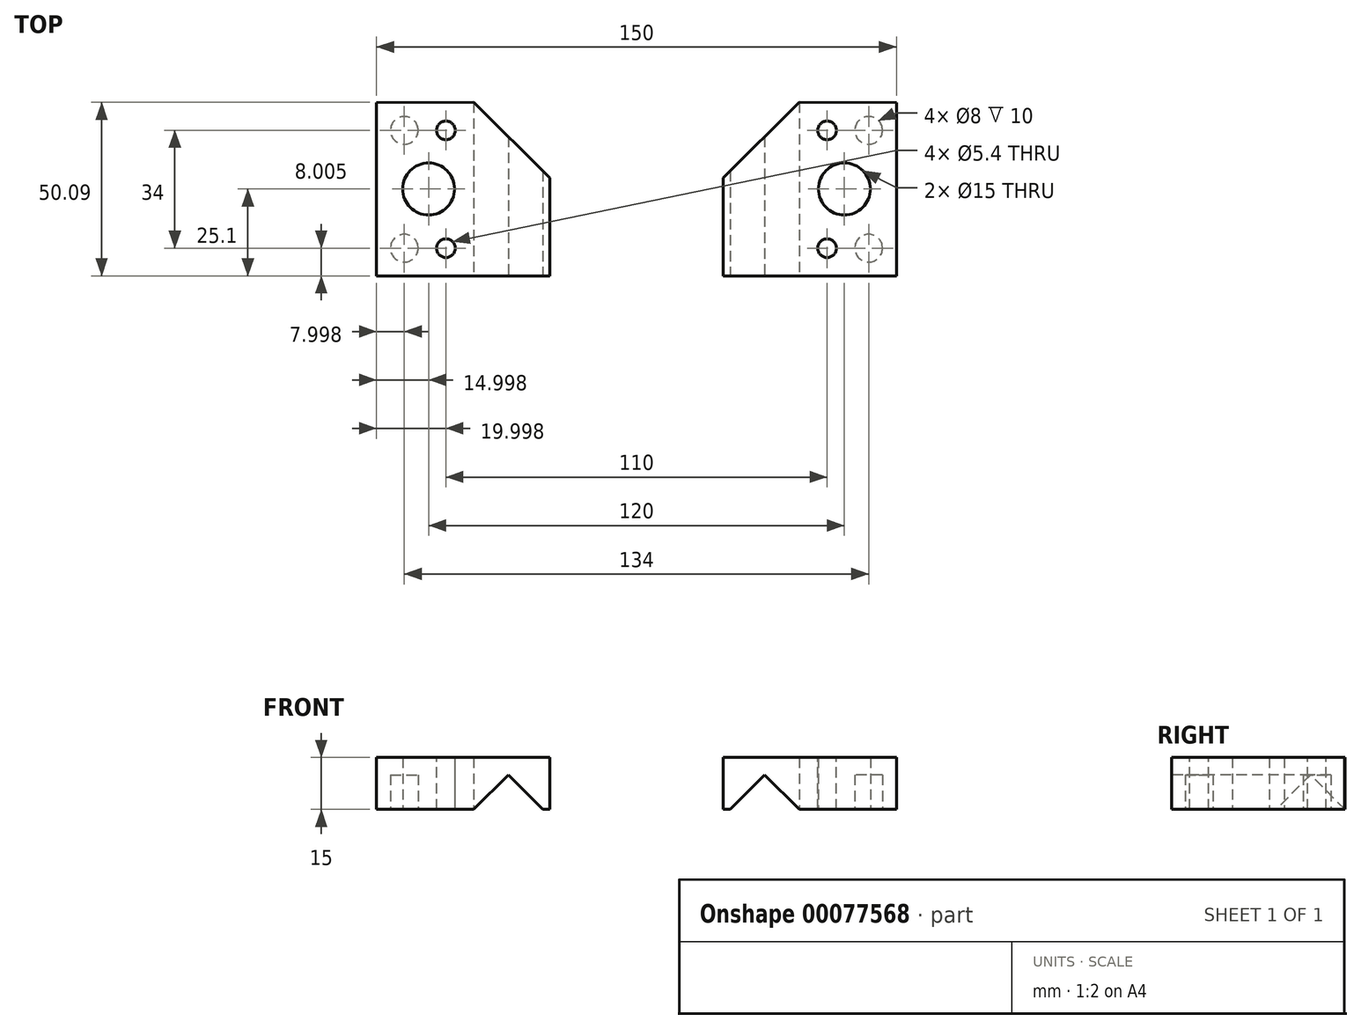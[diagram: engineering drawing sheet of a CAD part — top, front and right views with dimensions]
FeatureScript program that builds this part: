
annotation { "Feature Type Name" : "Feature", "Feature Type Description" : "" }
export const myFeature = defineFeature(function(context is Context, id is Id, definition is map)
    precondition{}
    {
        {
            var Q0;
            Q0=qCreatedBy(makeId("Top.planeOp"),FACE);
            var sketch = newSketch(context, id + "F0", { "sketchPlane" : qUnion([Q0])});
            skLineSegment(sketch, "E0.bottom", {"start": v(24.6, 20.06) * mm, "end": v(-25.4, 19.9) * mm});
            skLineSegment(sketch, "E0.top", {"start": v(24.6, -30.1) * mm, "end": v(-25.4, -30.1) * mm});
            skLineSegment(sketch, "E0.left", {"start": v(24.6, 20.06) * mm, "end": v(24.6, -30.1) * mm});
            skLineSegment(sketch, "E0.right", {"start": v(-25.4, 19.9) * mm, "end": v(-25.4, -30.1) * mm});
            skPoint(sketch, "E0.middle", {"position": v(0, 0) * mm});
            skSolve(sketch);
        }
        {
            var Q0;
            Q0 = qSketchRegion(id + "F0", true);
            extrude(context, id + "F1", {"entities" : qUnion([Q0]), "depth" : 15 * mm});
        }
        {
            var Q0;
            Q0=makeQuery(id+"F1.opExtrude","SWEPT_FACE",FACE,{"disambiguationData":[OSD([sQuery(id+"F0.wireOp",EDGE,"E0.top")])]});
            var sketch = newSketch(context, id + "F2", { "sketchPlane" : qUnion([Q0])});
            skLineSegment(sketch, "E1", {"start": v(22.6, 0) * mm, "end": v(12.6, 10) * mm});
            skPoint(sketch, "E1.endSnap0", {"position": v(20, 12.5) * mm});
            skLineSegment(sketch, "E2", {"start": v(12.6, 10) * mm, "end": v(2.6, 0) * mm});
            skLineSegment(sketch, "E3", {"start": v(2.6, 0) * mm, "end": v(22.6, 0) * mm});
            skSolve(sketch);
        }
        {
            var Q0;
            Q0=makeQuery(id+"F2.imprint","IMPRINT",FACE,{"disambiguationData":[TD([[makeQuery(id+"F2.imprint","IMPRINT",EDGE,{"derivedFrom":sQuery(id+"F2.wireOp",EDGE,"E1")}),1.0]])]});
            extrude(context, id + "F3", {"entities" : qUnion([Q0]), "operationType" : NewBodyOperationType.REMOVE, "endBound" : BoundingType.THROUGH_ALL, "oppositeDirection" : true, "depth" : 25 * mm});
        }
        {
            var Q0;
            {var subQ0=sQuery(id+"F0.wireOp",EDGE,"E0.bottom");var subQ1=sQuery(id+"F0.wireOp",EDGE,"E0.top");var subQ2=sQuery(id+"F0.wireOp",EDGE,"E0.right");Q0=makeQuery(id+"F3.boolean.opBoolean","SPLIT",FACE,{"disambiguationData":[TD([makeQuery(id+"F1.opExtrude","SWEPT_FACE",FACE,{"disambiguationData":[OSD([subQ2])]})])],"derivedFrom":makeQuery(id+"F1.opExtrude","CAP_FACE",FACE,{"disambiguationData":[OSD([subQ0,subQ1,sQuery(id+"F0.wireOp",EDGE,"E0.left"),subQ2])],"isStart":true})});}
            var sketch = newSketch(context, id + "F4", { "sketchPlane" : qUnion([Q0])});
            skCircle(sketch, "E4", {"center": v(-17.4, 22.1) * mm, "radius": 4 * mm});
            skCircle(sketch, "E5", {"center": v(-17.4, -11.9) * mm, "radius": 4 * mm});
            skSolve(sketch);
        }
        {
            var Q0;
            Q0 = qSketchRegion(id + "F4", true);
            extrude(context, id + "F5", {"entities" : qUnion([Q0]), "operationType" : NewBodyOperationType.REMOVE, "oppositeDirection" : true, "depth" : 10 * mm});
        }
        {
            var Q0;
            {var subQ0=sQuery(id+"F0.wireOp",EDGE,"E0.bottom");var subQ1=sQuery(id+"F0.wireOp",EDGE,"E0.top");var subQ2=sQuery(id+"F0.wireOp",EDGE,"E0.right");Q0=makeQuery(id+"F3.boolean.opBoolean","SPLIT",FACE,{"disambiguationData":[TD([makeQuery(id+"F1.opExtrude","SWEPT_FACE",FACE,{"disambiguationData":[OSD([subQ2])]})])],"derivedFrom":makeQuery(id+"F1.opExtrude","CAP_FACE",FACE,{"disambiguationData":[OSD([subQ0,subQ1,sQuery(id+"F0.wireOp",EDGE,"E0.left"),subQ2])],"isStart":true})});}
            var sketch = newSketch(context, id + "F6", { "sketchPlane" : qUnion([Q0])});
            skLineSegment(sketch, "E6", {"start": v(-10.4, 22) * mm, "end": v(-10.4, -12) * mm});
            skLineSegment(sketch, "E7", {"start": v(-4.4, 0) * mm, "end": v(-10.4, 5) * mm});
            skPoint(sketch, "E8", {"position": v(-10.4, 5) * mm});
            skPoint(sketch, "E9", {"position": v(3.86, -3.22) * mm});
            skCircle(sketch, "E10", {"center": v(-10.4, 5) * mm, "radius": 7.5 * mm});
            skLineSegment(sketch, "E11", {"start": v(-6, 12.5) * mm, "end": v(-23, 12.5) * mm});
            skLineSegment(sketch, "E12", {"start": v(-6, -2.5) * mm, "end": v(-23, -2.5) * mm});
            skSolve(sketch);
        }
        {
            var Q0;
            {var subQ0=sQuery(id+"F6.wireOp",EDGE,"E6");var subQ1=makeQuery(id+"F6.imprint","INTERSECT",VERTEX,{"derivedFrom":[subQ0,sQuery(id+"F6.wireOp",EDGE,"E7")]});Q0=makeQuery(id+"F6.imprint","IMPRINT",FACE,{"disambiguationData":[TD([[makeQuery(id+"F6.imprint","IMPRINT",EDGE,{"disambiguationData":[TD([[subQ1,1.0]])],"derivedFrom":subQ0}),-1.0]])]});}
            var Q1;
            {var subQ0=sQuery(id+"F6.wireOp",EDGE,"E7");var subQ1=sQuery(id+"F6.wireOp",EDGE,"E6");var subQ2=makeQuery(id+"F6.imprint","INTERSECT",VERTEX,{"derivedFrom":[subQ1,subQ0]});Q1=makeQuery(id+"F6.imprint","IMPRINT",FACE,{"disambiguationData":[TD([[makeQuery(id+"F6.imprint","IMPRINT",EDGE,{"disambiguationData":[TD([[subQ2,1.0]])],"derivedFrom":subQ0}),-1.0]])]});}
            var Q2;
            {var subQ0=sQuery(id+"F6.wireOp",EDGE,"E7");var subQ1=sQuery(id+"F6.wireOp",EDGE,"E6");var subQ2=makeQuery(id+"F6.imprint","INTERSECT",VERTEX,{"derivedFrom":[subQ1,subQ0]});Q2=makeQuery(id+"F6.imprint","IMPRINT",FACE,{"disambiguationData":[TD([[makeQuery(id+"F6.imprint","IMPRINT",EDGE,{"disambiguationData":[TD([[subQ2,1.0]])],"derivedFrom":subQ0}),1.0]])]});}
            var Q3;
            {var subQ0=sQuery(id+"F6.wireOp",EDGE,"E6");var subQ1=makeQuery(id+"F6.imprint","IMPRINT",VERTEX,{"derivedFrom":subQ0});Q3=makeQuery(id+"F6.imprint","IMPRINT",FACE,{"disambiguationData":[TD([[makeQuery(id+"F6.imprint","IMPRINT",EDGE,{"disambiguationData":[TD([[subQ1,1.0]])],"derivedFrom":subQ0}),1.0]])]});}
            extrude(context, id + "F7", {"entities" : qUnion([Q0, Q1, Q2, Q3]), "operationType" : NewBodyOperationType.REMOVE, "endBound" : BoundingType.THROUGH_ALL, "oppositeDirection" : true, "depth" : 25 * mm});
        }
        {
            var Q0;
            Q0=makeQuery(id+"F1.opExtrude","CAP_FACE",FACE,{"disambiguationData":[OSD([sQuery(id+"F0.wireOp",EDGE,"E0.bottom"),sQuery(id+"F0.wireOp",EDGE,"E0.top"),sQuery(id+"F0.wireOp",EDGE,"E0.left"),sQuery(id+"F0.wireOp",EDGE,"E0.right")])],"isStart":false});
            var sketch = newSketch(context, id + "F8", { "sketchPlane" : qUnion([Q0])});
            skPoint(sketch, "E13.positionSnap0", {"position": v(-5.4, -22.1) * mm});
            skLineSegment(sketch, "E14", {"start": v(-5.4, -22.1) * mm, "end": v(-5.4, 11.9) * mm});
            skPoint(sketch, "E15", {"position": v(-5.4, 11.9) * mm});
            skSolve(sketch);
        }
        {
            var Q0;
            Q0=sQuery(id+"F8.wireOp",VERTEX,"E13.positionSnap0");
            var Q1;
            Q1=sQuery(id+"F8.wireOp",VERTEX,"E15");
            var Q2;
            Q2=makeQuery(id+"F1.opExtrude","SWEPT_BODY",BODY,{"disambiguationData":[OSD([sQuery(id+"F0.wireOp",EDGE,"E0.bottom"),sQuery(id+"F0.wireOp",EDGE,"E0.top"),sQuery(id+"F0.wireOp",EDGE,"E0.left"),sQuery(id+"F0.wireOp",EDGE,"E0.right")])]});
            hole(context, id + "F9", {"style" : HoleStyle.SIMPLE, "endStyle" : HoleEndStyle.BLIND, "standardTappedOrClearance" : lookupTablePath({ "standard" : "ISO", "engagement" : "25%", "pitch" : "1 mm", "size" : "M6", "type" : "Tapped" }), "standardBlindInLast" : lookupTablePath({ "standard" : "ISO", "engagement" : "25%", "pitch" : "1 mm", "size" : "M6", "type" : "Tapped" }), "holeDiameter" : 5.4 * mm, "holeDepth" : 60 * mm, "startFromSketch" : true, "locations" : qUnion([Q0, Q1]), "scope" : qUnion([Q2])});
        }
        {
            var Q0;
            {var subQ0=sQuery(id+"F0.wireOp",EDGE,"E0.bottom");var subQ1=sQuery(id+"F0.wireOp",EDGE,"E0.top");var subQ2=sQuery(id+"F0.wireOp",EDGE,"E0.right");Q0=makeQuery(id+"F3.boolean.opBoolean","SPLIT",FACE,{"disambiguationData":[TD([makeQuery(id+"F1.opExtrude","SWEPT_FACE",FACE,{"disambiguationData":[OSD([subQ2])]})])],"derivedFrom":makeQuery(id+"F1.opExtrude","CAP_FACE",FACE,{"disambiguationData":[OSD([subQ0,subQ1,sQuery(id+"F0.wireOp",EDGE,"E0.left"),subQ2])],"isStart":true})});}
            var sketch = newSketch(context, id + "F10", { "sketchPlane" : qUnion([Q0])});
            skLineSegment(sketch, "E16", {"start": v(2.6, -20) * mm, "end": v(27.6, -20.07) * mm});
            skLineSegment(sketch, "E17", {"start": v(27.6, -20.07) * mm, "end": v(27.69, 4.93) * mm});
            skLineSegment(sketch, "E18", {"start": v(27.69, 4.93) * mm, "end": v(2.6, -20) * mm});
            skSolve(sketch);
        }
        {
            var Q0;
            Q0 = qSketchRegion(id + "F10", true);
            extrude(context, id + "F11", {"entities" : qUnion([Q0]), "operationType" : NewBodyOperationType.REMOVE, "endBound" : BoundingType.THROUGH_ALL, "oppositeDirection" : true, "depth" : 25 * mm});
        }
        {
            var Q0;
            Q0=makeQuery(id+"F1.opExtrude","SWEPT_BODY",BODY,{"disambiguationData":[OSD([sQuery(id+"F0.wireOp",EDGE,"E0.bottom"),sQuery(id+"F0.wireOp",EDGE,"E0.top"),sQuery(id+"F0.wireOp",EDGE,"E0.left"),sQuery(id+"F0.wireOp",EDGE,"E0.right")])]});
            var Q1;
            Q1=makeQuery(id+"F1.opExtrude","SWEPT_FACE",FACE,{"disambiguationData":[OSD([sQuery(id+"F0.wireOp",EDGE,"E0.left")])]});
            mirror(context, id + "F12", {"entities" : qUnion([Q0]), "mirrorPlane" : qUnion([Q1])});
        }
        {
            var Q0;
            Q0=makeQuery(id+"F12.opPattern","COPY",BODY,{"derivedFrom":makeQuery(id+"F1.opExtrude","SWEPT_BODY",BODY,{"disambiguationData":[OSD([sQuery(id+"F0.wireOp",EDGE,"E0.bottom"),sQuery(id+"F0.wireOp",EDGE,"E0.top"),sQuery(id+"F0.wireOp",EDGE,"E0.left"),sQuery(id+"F0.wireOp",EDGE,"E0.right")])]}),"instanceName":"1"});
            transform(context, id + "F13", {"entities" : qUnion([Q0]), "transformType" : TransformType.TRANSLATION_3D, "dx" : 50 * mm, "dy" : 0 * mm, "dz" : 0 * mm, "makeCopy" : false});
        }
    });
